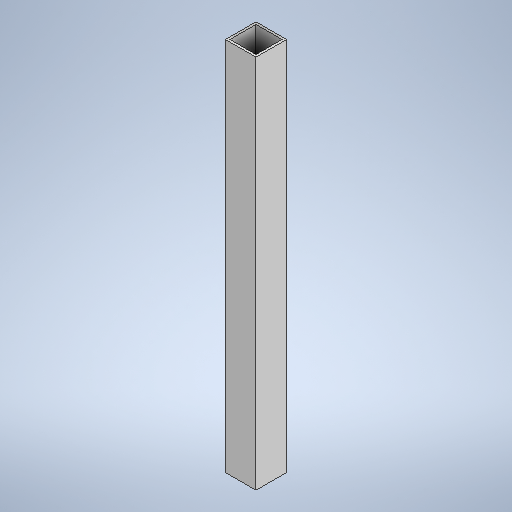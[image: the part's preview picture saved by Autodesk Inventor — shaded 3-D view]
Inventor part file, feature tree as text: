
AUTODESK INVENTOR PART (.ipt)
format: ipt  version: 2025 (Build 290162000, 162)  size: 255,488 bytes
history: native  units: in
note: dims shown in document units (in); Inventor stores cm internally (conversion verified against a paired STEP export)
features: extrude x1, sketch x1
ambient origin geometry x8: Origin, YZ Plane, XZ Plane, XY Plane, X Axis, Y Axis, Z Axis, Center Point
bodies: Solid1 (feature_tree)
feature tree (2):
  extrude  "Extrusion1"  Depth=1.5748in
  sketch  "Sketch1"  dims[d0=1.5748in d1=1.5748in d2=1.3386in d3=1.3386in d4=0.1181in d5=19.2913in d6=0.0in]
